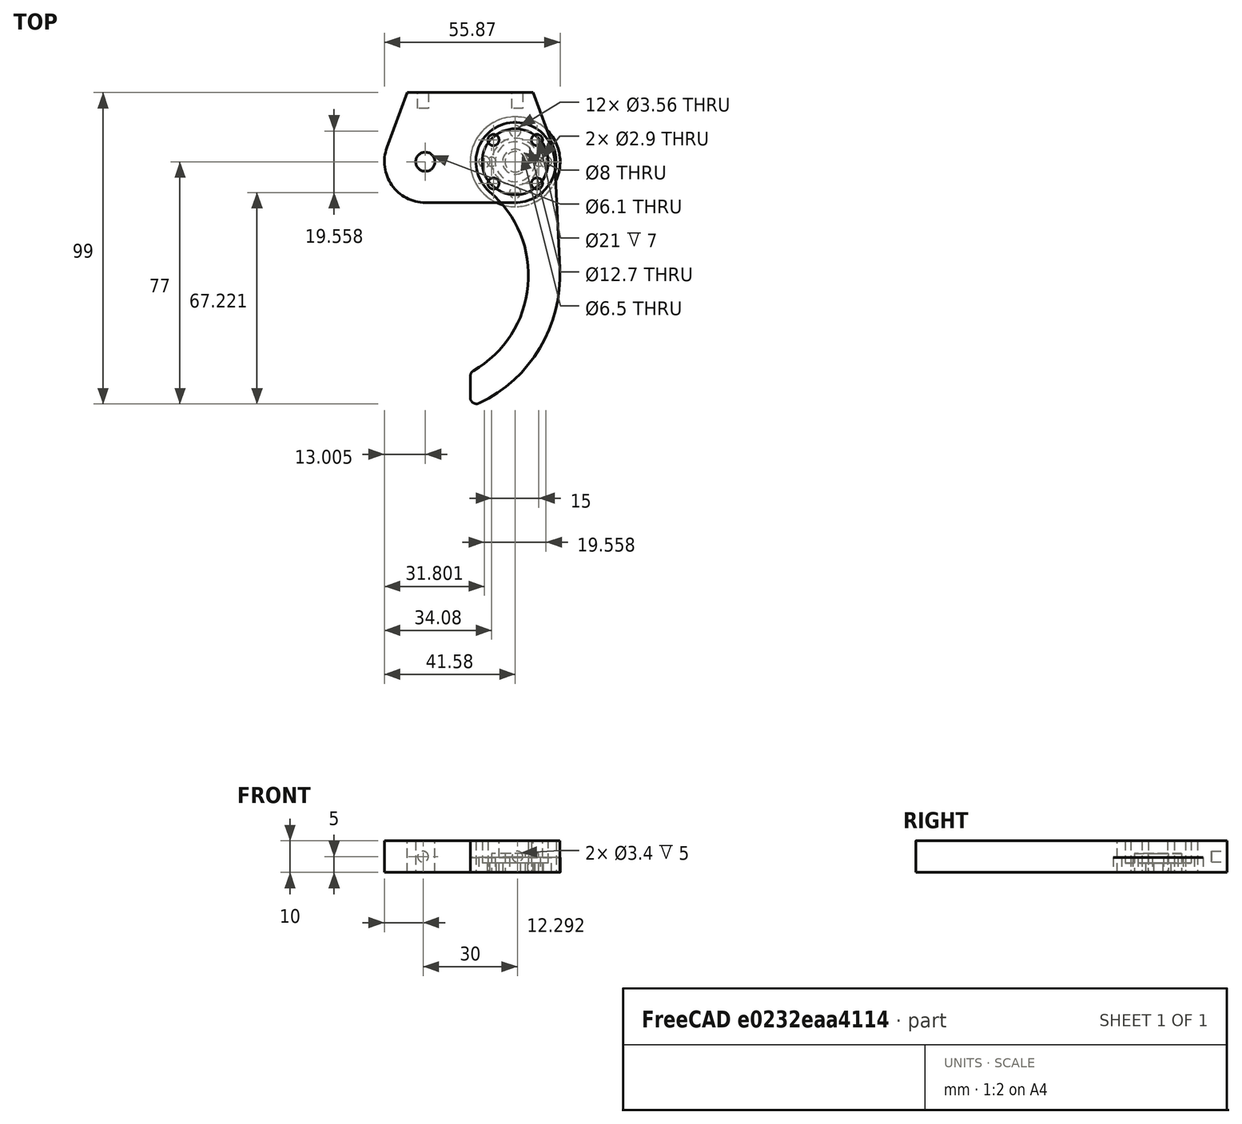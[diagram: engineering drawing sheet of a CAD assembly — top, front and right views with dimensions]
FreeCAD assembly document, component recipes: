
FREECAD ASSEMBLY — COMPONENT RECIPES ("A4-GRIPPER")

This assembly document has 4 components, labeled P0..P3 below (a component is one placed body or linked part). 4 of them carry a construction recipe — the FreeCAD feature program that regenerates the part from scratch, quoted from this document or its linked companion documents; the rest are supplied as boundary geometry only. No exploded tour is included for this assembly.
COMPONENT P0 — recipe-attached ("BASE_1_0", modeled in this document).
Construction recipe (the document's own serialized feature program — sketch geometry with constraints, then the solid features built on it; lengths are millimeters unless a unit is written):

FEATURE [PartDesign::CoordinateSystem] LCS_0005
  AttacherType = Attacher::AttachEngine3D
  MapMode = 2
  Support = -> [X_Axis006]
FEATURE [Sketcher::SketchObject] Sketch002
  FullyConstrained = true
  MapMode = 5
  Support = -> [XY_Plane006]
  sketch-geometry (10):
    g0: Circle CenterX=0 CenterY=0 CenterZ=0 NormalX=0 NormalY=0 NormalZ=1 AngleXU=0 Radius=4
    g1: Circle CenterX=7.5 CenterY=0 CenterZ=0 NormalX=0 NormalY=0 NormalZ=1 AngleXU=0 Radius=1.45
    g2: Circle CenterX=-7.5 CenterY=0 CenterZ=0 NormalX=0 NormalY=0 NormalZ=1 AngleXU=0 Radius=1.45
    g3: Circle CenterX=-28.575 CenterY=0 CenterZ=0 NormalX=0 NormalY=0 NormalZ=1 AngleXU=0 Radius=3.05
    g4: LineSegment StartX=-34.2875 StartY=22 StartZ=0 EndX=5.7125 EndY=22 EndZ=0
    g5: LineSegment StartX=5.7125 StartY=22 StartZ=0 EndX=12.1902 EndY=4.51652 EndZ=0
    g6: LineSegment StartX=-2.4e-15 StartY=-13 StartZ=0 EndX=-28.575 EndY=-13 EndZ=0
    g7: LineSegment StartX=-40.7652 StartY=4.51652 StartZ=0 EndX=-34.2875 EndY=22 EndZ=0
    g8: ArcOfCircle CenterX=0 CenterY=0 CenterZ=0 NormalX=0 NormalY=0 NormalZ=1 AngleXU=0 Radius=13 StartAngle=4.71239 EndAngle=6.63801
    g9: ArcOfCircle CenterX=-28.575 CenterY=0 CenterZ=0 NormalX=0 NormalY=0 NormalZ=1 AngleXU=0 Radius=13 StartAngle=2.78677 EndAngle=4.71239
  constraints (24):
    c: Coincident(g0,g-1)
    c: PointOnObject(g1,g-1)
    c: Diameter(g0) = 8
    c: DistanceX(g2,g1) = 15
    c: Diameter(g2) = 2.9
    c: Equal(g2,g1)
    c: Symmetric(g2,g1,g-2)
    c: PointOnObject(g3,g-1)
    c: Diameter(g3) = 6.1
    c: DistanceX(g3,g-1) = 28.575
    c: Coincident(g4,g5)
    c: Coincident(g7,g4)
    c: Horizontal(g4)
    c: Horizontal(g6)
    c: DistanceY(g-1,g4) = 22
    c: Tangent(g6,g8) = 1.5708
    c: Tangent(g5,g8) = 1.5708
    c: Tangent(g7,g9) = 1.5708
    c: Tangent(g6,g9) = 1.5708
    c: DistanceX(g4,g4) = 40
    c: Coincident(g8,g0)
    c: Coincident(g9,g3)
    c: Diameter(g8) = 26
    c: Horizontal(g7,g5)
FEATURE [PartDesign::Pad] Pad002
  Direction = (1,1,1)
  Length = 10
  Length2 = 100
  Profile = -> Sketch002
  Refine = true
  Type = 0
FEATURE [Sketcher::SketchObject] Sketch003
  AttachmentOffset = pos=(0,0,3) rot=(0,0,1;0rad)
  FullyConstrained = true
  MapMode = 5
  Placement = pos=(0,0,3) rot=(0,0,1;0rad)
  Support = -> [XY_Plane006]
  sketch-geometry (1):
    g0: Circle CenterX=0 CenterY=0 CenterZ=0 NormalX=0 NormalY=0 NormalZ=1 AngleXU=0 Radius=10.5
  constraints (2):
    c: Coincident(g0,g-1)
    c: Diameter(g0) = 21
FEATURE [PartDesign::Pocket] Pocket
  BaseFeature = -> Pad002
  Length = 7
  Length2 = 100
  Profile = -> Sketch003
  Refine = true
  Reversed = true
  Type = 0
FEATURE [Sketcher::SketchObject] Sketch004
  AttachmentOffset = pos=(0,0,-22) rot=(0,0,1;0rad)
  FullyConstrained = true
  MapMode = 5
  Placement = pos=(0,22,-4.9e-15) rot=(1,0,0;1.5708rad)
  Support = -> [XZ_Plane006]
  sketch-geometry (2):
    g0: Circle CenterX=-29.2875 CenterY=5 CenterZ=0 NormalX=0 NormalY=0 NormalZ=1 AngleXU=0 Radius=1.7
    g1: Circle CenterX=0.7125 CenterY=5 CenterZ=0 NormalX=0 NormalY=0 NormalZ=1 AngleXU=0 Radius=1.7
  constraints (6):
    c: Diameter(g1) = 3.4
    c: Equal(g1,g0)
    c: DistanceY(g-1,g0) = 5
    c: DistanceX(g0,g1) = 30
    c: Horizontal(g0,g1)
    c: DistanceX(g0,g-1) = 29.2875
FEATURE [PartDesign::Pocket] Pocket001
  BaseFeature = -> Pocket
  Length = 5
  Length2 = 100
  Profile = -> Sketch004
  Refine = true
  Reversed = true
  Type = 0
FEATURE [PartDesign::Body] Body_3
  Group = -> [LCS_0005,Sketch002,Pad002,Sketch003,Pocket,Sketch004,Pocket001]
  Origin = -> Origin006
  Tip = -> Pocket001
COMPONENT P1 — recipe-attached ("GEAR-RHA32-36-36", modeled in this document).
Construction recipe (the document's own serialized feature program — sketch geometry with constraints, then the solid features built on it; lengths are millimeters unless a unit is written):

FEATURE [PartDesign::CoordinateSystem] LCS_0001
  AttacherType = Attacher::AttachEngine3D
  MapMode = 2
  Support = -> [X_Axis002]
FEATURE [Sketcher::SketchObject] Sketch
  FullyConstrained = true
  MapMode = 5
  Support = -> [XY_Plane002]
  sketch-geometry (15):
    g0: Circle CenterX=0 CenterY=0 CenterZ=0 NormalX=0 NormalY=0 NormalZ=1 AngleXU=0 Radius=14.2875
    g1: Circle CenterX=0 CenterY=0 CenterZ=0 NormalX=0 NormalY=0 NormalZ=1 AngleXU=0 Radius=6.35
    g2: Circle CenterX=0 CenterY=0 CenterZ=0 NormalX=0 NormalY=0 NormalZ=1 AngleXU=0 Radius=9.779
    g3: Circle CenterX=-6.9148 CenterY=6.9148 CenterZ=0 NormalX=0 NormalY=0 NormalZ=1 AngleXU=0 Radius=1.778
    g4: Circle CenterX=0 CenterY=9.779 CenterZ=0 NormalX=0 NormalY=0 NormalZ=1 AngleXU=0 Radius=1.778
    g5: Circle CenterX=6.9148 CenterY=6.9148 CenterZ=0 NormalX=0 NormalY=0 NormalZ=1 AngleXU=0 Radius=1.778
    g6: Circle CenterX=9.779 CenterY=0 CenterZ=0 NormalX=0 NormalY=0 NormalZ=1 AngleXU=0 Radius=1.778
    g7: Circle CenterX=6.9148 CenterY=-6.9148 CenterZ=0 NormalX=0 NormalY=0 NormalZ=1 AngleXU=0 Radius=1.778
    g8: Circle CenterX=0 CenterY=-9.779 CenterZ=0 NormalX=0 NormalY=0 NormalZ=1 AngleXU=0 Radius=1.778
    g9: Circle CenterX=-6.9148 CenterY=-6.9148 CenterZ=0 NormalX=0 NormalY=0 NormalZ=1 AngleXU=0 Radius=1.778
    g10: Circle CenterX=-9.779 CenterY=0 CenterZ=0 NormalX=0 NormalY=0 NormalZ=1 AngleXU=0 Radius=1.778
    g11: LineSegment StartX=-6.9148 StartY=6.9148 StartZ=0 EndX=6.9148 EndY=6.9148 EndZ=0
    g12: LineSegment StartX=6.9148 StartY=6.9148 StartZ=0 EndX=6.9148 EndY=-6.9148 EndZ=0
    g13: LineSegment StartX=6.9148 StartY=-6.9148 StartZ=0 EndX=-6.9148 EndY=-6.9148 EndZ=0
    g14: LineSegment StartX=-6.9148 StartY=-6.9148 StartZ=0 EndX=-6.9148 EndY=6.9148 EndZ=0
  constraints (38):
    c: Coincident(g0,g-1)
    c: Diameter(g0) = 28.575
    c: Coincident(g1,g0)
    c: Diameter(g1) = 12.7
    c: Coincident(g2,g0)
    c: Diameter(g2) = 19.558
    c: PointOnObject(g3,g2)
    c: PointOnObject(g4,g2)
    c: PointOnObject(g5,g2)
    c: PointOnObject(g6,g2)
    c: PointOnObject(g7,g2)
    c: PointOnObject(g8,g2)
    c: PointOnObject(g9,g2)
    c: PointOnObject(g10,g2)
    c: PointOnObject(g10,g-1)
    c: Coincident(g11,g12)
    c: Coincident(g12,g13)
    c: Coincident(g13,g14)
    c: Coincident(g14,g11)
    c: Horizontal(g11)
    c: Horizontal(g13)
    c: Vertical(g12)
    c: Coincident(g11,g3)
    c: Coincident(g12,g7)
    c: Equal(g11,g14)
    c: Coincident(g13,g9)
    c: Coincident(g5,g11)
    c: PointOnObject(g4,g-2)
    c: PointOnObject(g6,g-1)
    c: PointOnObject(g8,g-2)
    c: Diameter(g4) = 3.556
    c: Equal(g4,g3)
    c: Equal(g4,g10)
    c: Equal(g4,g9)
    c: Equal(g4,g8)
    c: Equal(g4,g7)
    c: Equal(g4,g6)
    c: Equal(g4,g5)
FEATURE [PartDesign::Pad] Pad
  Direction = (1,1,1)
  Length = 4.7752
  Length2 = 100
  Profile = -> Sketch
  Refine = true
  Type = 0
FEATURE [PartDesign::Body] Body
  Group = -> [LCS_0001,Sketch,Pad]
  Origin = -> Origin002
  Tip = -> Pad
COMPONENT P2 — recipe-attached ("GRIPPER-DRIVEN-1.0", modeled in this document).
Construction recipe (the document's own serialized feature program — sketch geometry with constraints, then the solid features built on it; lengths are millimeters unless a unit is written):

FEATURE [PartDesign::CoordinateSystem] LCS_0003
  AttacherType = Attacher::AttachEngine3D
  MapMode = 2
  Support = -> [X_Axis004]
FEATURE [Sketcher::SketchObject] Sketch001
  FullyConstrained = true
  MapMode = 5
  Support = -> [XY_Plane004]
  sketch-geometry (18):
    g0: Circle CenterX=0 CenterY=0 CenterZ=0 NormalX=0 NormalY=0 NormalZ=1 AngleXU=0 Radius=9.779
    g1: LineSegment StartX=-6.9148 StartY=6.9148 StartZ=0 EndX=6.9148 EndY=6.9148 EndZ=0
    g2: LineSegment StartX=6.9148 StartY=6.9148 StartZ=0 EndX=6.9148 EndY=-6.9148 EndZ=0
    g3: LineSegment StartX=6.9148 StartY=-6.9148 StartZ=0 EndX=-6.9148 EndY=-6.9148 EndZ=0
    g4: LineSegment StartX=-6.9148 StartY=-6.9148 StartZ=0 EndX=-6.9148 EndY=6.9148 EndZ=0
    g5: Circle CenterX=-6.9148 CenterY=6.9148 CenterZ=0 NormalX=0 NormalY=0 NormalZ=1 AngleXU=0 Radius=1.778
    g6: Circle CenterX=6.9148 CenterY=6.9148 CenterZ=0 NormalX=0 NormalY=0 NormalZ=1 AngleXU=0 Radius=1.778
    g7: Circle CenterX=6.9148 CenterY=-6.9148 CenterZ=0 NormalX=0 NormalY=0 NormalZ=1 AngleXU=0 Radius=1.778
    g8: Circle CenterX=-6.9148 CenterY=-6.9148 CenterZ=0 NormalX=0 NormalY=0 NormalZ=1 AngleXU=0 Radius=1.778
    g9: ArcOfCircle CenterX=0 CenterY=0 CenterZ=0 NormalX=0 NormalY=0 NormalZ=1 AngleXU=0 Radius=12.5 StartAngle=0.048599 EndAngle=4.00747
    g10: ArcOfCircle CenterX=-30.7788 CenterY=-36.179 CenterZ=0 NormalX=0 NormalY=0 NormalZ=1 AngleXU=0 Radius=35 StartAngle=5.23572 EndAngle=7.14906
    g11: ArcOfCircle CenterX=-30.7788 CenterY=-36.179 CenterZ=0 NormalX=0 NormalY=0 NormalZ=1 AngleXU=0 Radius=45 StartAngle=5.15691 EndAngle=6.33178
    g12: LineSegment StartX=12.4852 StartY=0.607249 StartZ=0 EndX=14.1681 EndY=-33.9929 EndZ=0
    g13: Circle CenterX=0 CenterY=0 CenterZ=0 NormalX=0 NormalY=0 NormalZ=1 AngleXU=0 Radius=14.2875
    g14: ArcOfCircle CenterX=-12.2875 CenterY=-68.2269 CenterZ=0 NormalX=0 NormalY=0 NormalZ=1 AngleXU=0 Radius=2 StartAngle=2.09412 EndAngle=3.14159
    g15: ArcOfCircle CenterX=-12.2875 CenterY=-75 CenterZ=0 NormalX=0 NormalY=0 NormalZ=1 AngleXU=0 Radius=2 StartAngle=3.14159 EndAngle=5.15691
    g16: LineSegment StartX=-14.2875 StartY=-75 StartZ=0 EndX=-14.2875 EndY=-68.2269 EndZ=0
    g17: LineSegment StartX=-14.2875 StartY=0 StartZ=0 EndX=-14.2875 EndY=-68.2269 EndZ=0
  constraints (44):
    c: Coincident(g0,g-1)
    c: Diameter(g0) = 19.558
    c: Coincident(g1,g2)
    c: Coincident(g2,g3)
    c: Coincident(g3,g4)
    c: Coincident(g4,g1)
    c: Horizontal(g1)
    c: Horizontal(g3)
    c: Vertical(g2)
    c: Vertical(g4)
    c: PointOnObject(g1,g0)
    c: PointOnObject(g2,g0)
    c: Equal(g1,g4)
    c: PointOnObject(g1,g0)
    c: Coincident(g5,g1)
    c: Coincident(g6,g1)
    c: Coincident(g7,g2)
    c: Coincident(g8,g3)
    c: Diameter(g7) = 3.556
    c: Equal(g7,g8)
    c: Equal(g7,g5)
    c: Equal(g7,g6)
    c: Coincident(g9,g-1)
    c: Diameter(g9) = 25
    c: Coincident(g11,g10)
    c: Tangent(g12,g11) = 1.5708
    c: Diameter(g10) = 70
    c: Diameter(g11) = 90
    c: Coincident(g13,g9)
    c: Diameter(g13) = 28.575
    c: Tangent(g9,g12) = 1.5708
    c: Tangent(g9,g10) = 1.5708
    c: Tangent(g10,g14) = 1.5708
    c: Tangent(g11,g15) = -1.5708
    c: Vertical(g16)
    c: PointOnObject(g17,g13)
    c: Coincident(g17,g14)
    c: Vertical(g17)
    c: PointOnObject(g17,g-1)
    c: Diameter(g14) = 4
    c: Equal(g14,g15)
    c: Tangent(g16,g15) = 1.5708
    c: Tangent(g16,g14) = 1.5708
    c: DistanceY(g15,g-1) = 75
FEATURE [PartDesign::Pad] Pad001
  Direction = (1,1,1)
  Length = 10
  Length2 = 100
  Profile = -> Sketch001
  Refine = true
  Type = 0
FEATURE [PartDesign::Body] Body_2
  Group = -> [LCS_0003,Sketch001,Pad001]
  Origin = -> Origin004
  Tip = -> Pad001
COMPONENT P3 — recipe-attached ("SPACER_1_0", modeled in this document).
Construction recipe (the document's own serialized feature program — sketch geometry with constraints, then the solid features built on it; lengths are millimeters unless a unit is written):

FEATURE [PartDesign::CoordinateSystem] LCS_0007
  AttacherType = Attacher::AttachEngine3D
  MapMode = 2
  Support = -> [X_Axis008]
FEATURE [Sketcher::SketchObject] Sketch005
  FullyConstrained = true
  MapMode = 5
  Support = -> [XY_Plane008]
  sketch-geometry (2):
    g0: Circle CenterX=0 CenterY=0 CenterZ=0 NormalX=0 NormalY=0 NormalZ=1 AngleXU=0 Radius=3.25
    g1: Circle CenterX=0 CenterY=0 CenterZ=0 NormalX=0 NormalY=0 NormalZ=1 AngleXU=0 Radius=7.5
  constraints (4):
    c: Coincident(g0,g-1)
    c: Coincident(g1,g0)
    c: Diameter(g0) = 6.5
    c: Diameter(g1) = 15
FEATURE [PartDesign::Pad] Pad003
  Direction = (1,1,1)
  Length = 6
  Length2 = 100
  Profile = -> Sketch005
  Refine = true
  Type = 0
FEATURE [PartDesign::Body] Body_4
  Group = -> [LCS_0007,Sketch005,Pad003]
  Origin = -> Origin008
  Tip = -> Pad003
PROVENANCE & LICENSES
A FreeCAD (.FCStd) document from a public repository crawl; recipes are the document's own serialized feature recipes (and, for linked parts, companion documents' recipes).
License: as declared in the source repository (recorded in the dataset sidecar).
